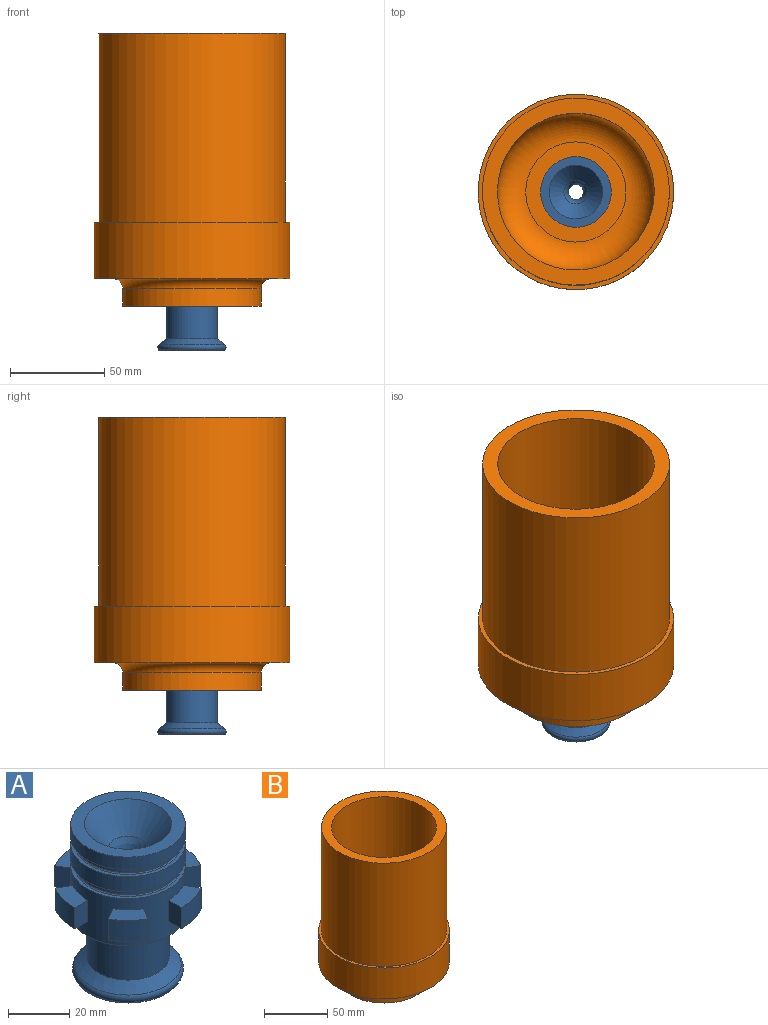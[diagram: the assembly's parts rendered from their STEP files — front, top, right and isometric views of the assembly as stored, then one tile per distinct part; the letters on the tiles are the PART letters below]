
ASSEMBLY  parts=2 mates=1
PART A: 55 faces, bbox 49.3x49.3x59.1 mm
  f0: cylinder r=24.65mm len=9.14mm, axis (0,0,1), area 109.5mm2, adj f1,f2,f44,f54
  f1: plane 12.08x12.06mm, normal (0,0,1), area 68.2mm2, adj f0,f34,f44,f54
  f2: plane 12.08x12.06mm, normal (0,0,-1), area 68.2mm2, adj f0,f34,f44,f54
  f3: cylinder r=24.65mm len=12.46mm, axis (0,0,1), area 109.5mm2, adj f4,f5,f52,f53
  f4: plane 12.46x8.46mm, normal (0,0,1), area 68.2mm2, adj f3,f34,f52,f53
  f5: plane 12.46x8.46mm, normal (0,0,-1), area 68.2mm2, adj f3,f34,f52,f53
  f6: cylinder r=24.65mm len=12.44mm, axis (0,0,1), area 109.5mm2, adj f7,f8,f49,f51
  f7: plane 12.44x8.51mm, normal (0,0,1), area 68.2mm2, adj f6,f34,f49,f51
  f8: plane 12.44x8.51mm, normal (0,0,-1), area 68.2mm2, adj f6,f34,f49,f51
  f9: cylinder r=24.65mm len=9.14mm, axis (0,0,1), area 109.5mm2, adj f10,f11,f48,f50
  f10: plane 12.08x12.06mm, normal (0,0,1), area 68.2mm2, adj f9,f34,f48,f50
  f11: plane 12.08x12.06mm, normal (0,0,-1), area 68.2mm2, adj f9,f34,f48,f50
  f12: cylinder r=24.65mm len=12.46mm, axis (0,0,1), area 109.5mm2, adj f13,f14,f46,f47
  f13: plane 12.46x8.46mm, normal (0,0,1), area 68.2mm2, adj f12,f34,f46,f47
  f14: plane 12.46x8.46mm, normal (0,0,-1), area 68.2mm2, adj f12,f34,f46,f47
  f15: cylinder r=4mm len=11.26mm, axis (0,0,1), area 282.9mm2, adj f16,f42
  f16: torus R=14mm, axis (0,0,1), area 210.2mm2, adj f15,f17
  f17: cone r=14.22mm half-angle=40deg, axis (0,0,1), area 791.5mm2, adj f16,f18
  f18: plane 37.4x37.4mm, normal (0,0,1), area 463.6mm2, adj f17,f19
  f19: cylinder r=18.7mm len=37.4mm, axis (0,0,1), area 587.5mm2, adj f18,f20
  f20: plane 37.4x37.4mm, normal (0,0,-1), area 145.2mm2, adj f19,f21
  f21: torus R=17.42mm, axis (0,0,1), area 67.8mm2, adj f20,f22
  f22: cylinder r=17.02mm len=34.04mm, axis (0,0,1), area 213.9mm2, adj f21,f23
  f23: torus R=17.42mm, axis (0,0,1), area 67.8mm2, adj f22,f24
  f24: plane 37.4x37.4mm, normal (0,0,1), area 145.2mm2, adj f23,f25
  f25: cylinder r=18.7mm len=37.4mm, axis (0,0,1), area 705mm2, adj f24,f26
  f26: plane 37.4x37.4mm, normal (0,0,-1), area 145.2mm2, adj f25,f27
  f27: torus R=17.42mm, axis (0,0,1), area 67.8mm2, adj f26,f28
  f28: cylinder r=17.02mm len=34.04mm, axis (0,0,1), area 213.9mm2, adj f27,f29
  f29: torus R=17.42mm, axis (0,0,1), area 67.8mm2, adj f28,f30
  f30: plane 37.4x37.4mm, normal (0,0,1), area 145.2mm2, adj f29,f34
  f31: plane 12.44x8.51mm, normal (0,0,1), area 68.2mm2, adj f32,f34,f43,f45
  f32: cylinder r=24.65mm len=12.44mm, axis (0,0,1), area 109.5mm2, adj f31,f33,f43,f45
  f33: plane 12.44x8.51mm, normal (0,0,-1), area 68.2mm2, adj f32,f34,f43,f45
  f34: cylinder r=18.7mm len=37.4mm, axis (0,0,1), area 1722.1mm2, adj f1,f2,f4,f5,f7,f8,f10,f11
  f35: plane 37.4x37.4mm, normal (0,0,-1), area 526mm2, adj f34,f36
  f36: cylinder r=13.5mm len=27mm, axis (0,0,1), area 1467.4mm2, adj f35,f37
  f37: cone r=17.38mm half-angle=50deg, axis (0,0,-1), area 490.7mm2, adj f36,f38
  f38: torus R=16.09mm, axis (0,0,1), area 314.1mm2, adj f37,f39
  f39: cone r=17.5mm half-angle=30deg, axis (0,0,1), area 71.3mm2, adj f38,f40
  f40: plane 35x35mm, normal (0,0,-1), area 678.6mm2, adj f39,f41
  f41: cone r=4.15mm half-angle=10deg, axis (0,0,-1), area 1320.9mm2, adj f40,f42
  f42: torus R=14mm, axis (0,0,1), area 44.4mm2, adj f15,f41
  f43: plane 8.4x5.95mm, normal (1,0,0), area 50mm2, adj f31,f32,f33,f34
  f44: plane 8.4x5.17mm, normal (-0.87,0.5,0), area 50mm2, adj f0,f1,f2,f34
  f45: plane 8.4x5.14mm, normal (-0.86,-0.5,0), area 50mm2, adj f31,f32,f33,f34
  f46: plane 8.4x5.15mm, normal (0.5,0.87,0), area 50mm2, adj f12,f13,f14,f34
  f47: plane 8.4x5.95mm, normal (0.01,-1,0), area 50mm2, adj f12,f13,f14,f34
  f48: plane 8.4x5.15mm, normal (-0.5,0.87,0), area 50mm2, adj f9,f10,f11,f34
  f49: plane 8.4x5.95mm, normal (-1,0,0), area 50mm2, adj f6,f7,f8,f34
  f50: plane 8.4x5.17mm, normal (0.87,-0.5,0), area 50mm2, adj f9,f10,f11,f34
  f51: plane 8.4x5.14mm, normal (0.86,0.5,0), area 50mm2, adj f6,f7,f8,f34
  f52: plane 8.4x5.15mm, normal (-0.5,-0.87,0), area 50mm2, adj f3,f4,f5,f34
  f53: plane 8.4x5.95mm, normal (-0.01,1,0), area 50mm2, adj f3,f4,f5,f34
  f54: plane 8.4x5.15mm, normal (0.5,-0.87,0), area 50mm2, adj f0,f1,f2,f34
PART B: 38 faces, bbox 103.5x103.5x144.5 mm
  f0: plane 73.5x73.5mm, normal (0,0,-1), area 2735.3mm2, adj f1,f3,f5,f7,f10,f12,f24,f25
  f1: cylinder r=18.7mm len=6.84mm, axis (0,0,1), area 58.7mm2, adj f0,f11,f26,f37
  f2: plane 12.35x8.51mm, normal (0,0,1), area 68.2mm2, adj f3,f12,f35,f36
  f3: cylinder r=18.7mm len=9.35mm, axis (0,0,1), area 58.7mm2, adj f0,f2,f35,f36
  f4: plane 12.35x8.51mm, normal (0,0,1), area 68.2mm2, adj f5,f12,f33,f34
  f5: cylinder r=18.7mm len=9.35mm, axis (0,0,1), area 58.7mm2, adj f0,f4,f33,f34
  f6: plane 12.04x12.04mm, normal (0,0,1), area 68.2mm2, adj f7,f12,f31,f32
  f7: cylinder r=18.7mm len=6.84mm, axis (0,0,1), area 58.7mm2, adj f0,f6,f31,f32
  f8: plane 12.35x8.51mm, normal (0,0,1), area 68.2mm2, adj f10,f12,f29,f30
  f9: plane 12.35x8.51mm, normal (0,0,1), area 68.2mm2, adj f12,f25,f27,f28
  f10: cylinder r=18.7mm len=9.35mm, axis (0,0,1), area 58.7mm2, adj f0,f8,f29,f30
  f11: plane 12.04x12.04mm, normal (0,0,1), area 68.2mm2, adj f1,f12,f26,f37
  f12: cylinder r=24.7mm len=49.4mm, axis (0,0,1), area 1784.7mm2, adj f0,f2,f4,f6,f8,f9,f11,f13
  f13: plane 49.4x49.4mm, normal (0,0,-1), area 818.1mm2, adj f12,f14
  f14: cylinder r=18.7mm len=37.4mm, axis (0,0,1), area 2467.4mm2, adj f13,f15
  f15: plane 53.06x53.06mm, normal (0,0,1), area 1112.6mm2, adj f14,f16
  f16: torus R=26.53mm, axis (0,0,1), area 5341.3mm2, adj f15,f17
  f17: cylinder r=41.53mm len=94mm, axis (0,0,1), area 24528.4mm2, adj f16,f18
  f18: plane 99.06x99.06mm, normal (0,0,1), area 2288.6mm2, adj f17,f19
  f19: cylinder r=49.53mm len=100mm, axis (0,0,1), area 31120.6mm2, adj f18,f20
  f20: plane 103.5x103.5mm, normal (0,0,1), area 706.4mm2, adj f19,f21
  f21: cylinder r=51.75mm len=103.5mm, axis (0,0,1), area 9754.6mm2, adj f20,f22
  f22: plane 103.5x103.5mm, normal (0,0,-1), area 2937.4mm2, adj f21,f23
  f23: torus R=41.75mm, axis (0,0,1), area 1903.2mm2, adj f22,f24
  f24: cylinder r=36.75mm len=73.5mm, axis (0,0,1), area 2193.6mm2, adj f0,f23
  f25: cylinder r=18.7mm len=9.35mm, axis (0,0,1), area 58.7mm2, adj f0,f9,f27,f28
  f26: plane 6x5.2mm, normal (0.87,-0.5,0), area 36mm2, adj f0,f1,f11,f12
  f27: plane 6x6mm, normal (-1,0,0), area 36mm2, adj f0,f9,f12,f25
  f28: plane 6x5.2mm, normal (0.87,0.5,0), area 36mm2, adj f0,f9,f12,f25
  f29: plane 6x5.2mm, normal (-0.5,-0.87,0), area 36mm2, adj f0,f8,f10,f12
  f30: plane 6x6mm, normal (0,1,0), area 36mm2, adj f0,f8,f10,f12
  f31: plane 6x5.2mm, normal (0.5,-0.87,0), area 36mm2, adj f0,f6,f7,f12
  f32: plane 6x5.2mm, normal (-0.87,0.5,0), area 36mm2, adj f0,f6,f7,f12
  f33: plane 6x6mm, normal (1,0,0), area 36mm2, adj f0,f4,f5,f12
  f34: plane 6x5.2mm, normal (-0.87,-0.5,0), area 36mm2, adj f0,f4,f5,f12
  f35: plane 6x5.2mm, normal (0.5,0.87,0), area 36mm2, adj f0,f2,f3,f12
  f36: plane 6x6mm, normal (0,-1,0), area 36mm2, adj f0,f2,f3,f12
  f37: plane 6x5.2mm, normal (-0.5,0.87,0), area 36mm2, adj f0,f1,f11,f12
PLACE A t=(-40.23,-0.35,-37.83)mm
PLACE B t=(-40.23,-0.35,-23.43)mm fixed
MATE cylindrical B.f1 <-> A.f0  axis (0,0,-1) through (-40.23,-0.35,-37.93)mm
